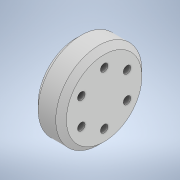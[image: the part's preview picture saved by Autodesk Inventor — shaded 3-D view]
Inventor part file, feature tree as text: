
AUTODESK INVENTOR PART (.ipt)
format: ipt  version: 2022 (Build 260153000, 153)  size: 175,616 bytes
history: native  units: mm
features: sketch x4, revolve x2, hole x2, other x1, thread x1
ambient origin geometry x8: Origin, YZ Plane, XZ Plane, XY Plane, X Axis, Y Axis, Z Axis, Center Point
bodies: Body1 (feature_tree)
feature tree (10):
  other  "Твердое тело1"
  revolve  "Вращение1"
  revolve  "Вращение2"
  hole  "Отверстие1"  [1 undecoded]
  hole  "Отверстие2"  [1 undecoded]
  thread  "Резьба1"
  sketch  "Эскиз1"
  sketch  "Эскиз2"
  sketch  "Эскиз3"
  sketch  "Эскиз4"
note: 2 required parameter values undecoded (feature->parameter linkage not recoverable at this tier; creation-order binding heuristic only, values carry confidence <= 0.55)
